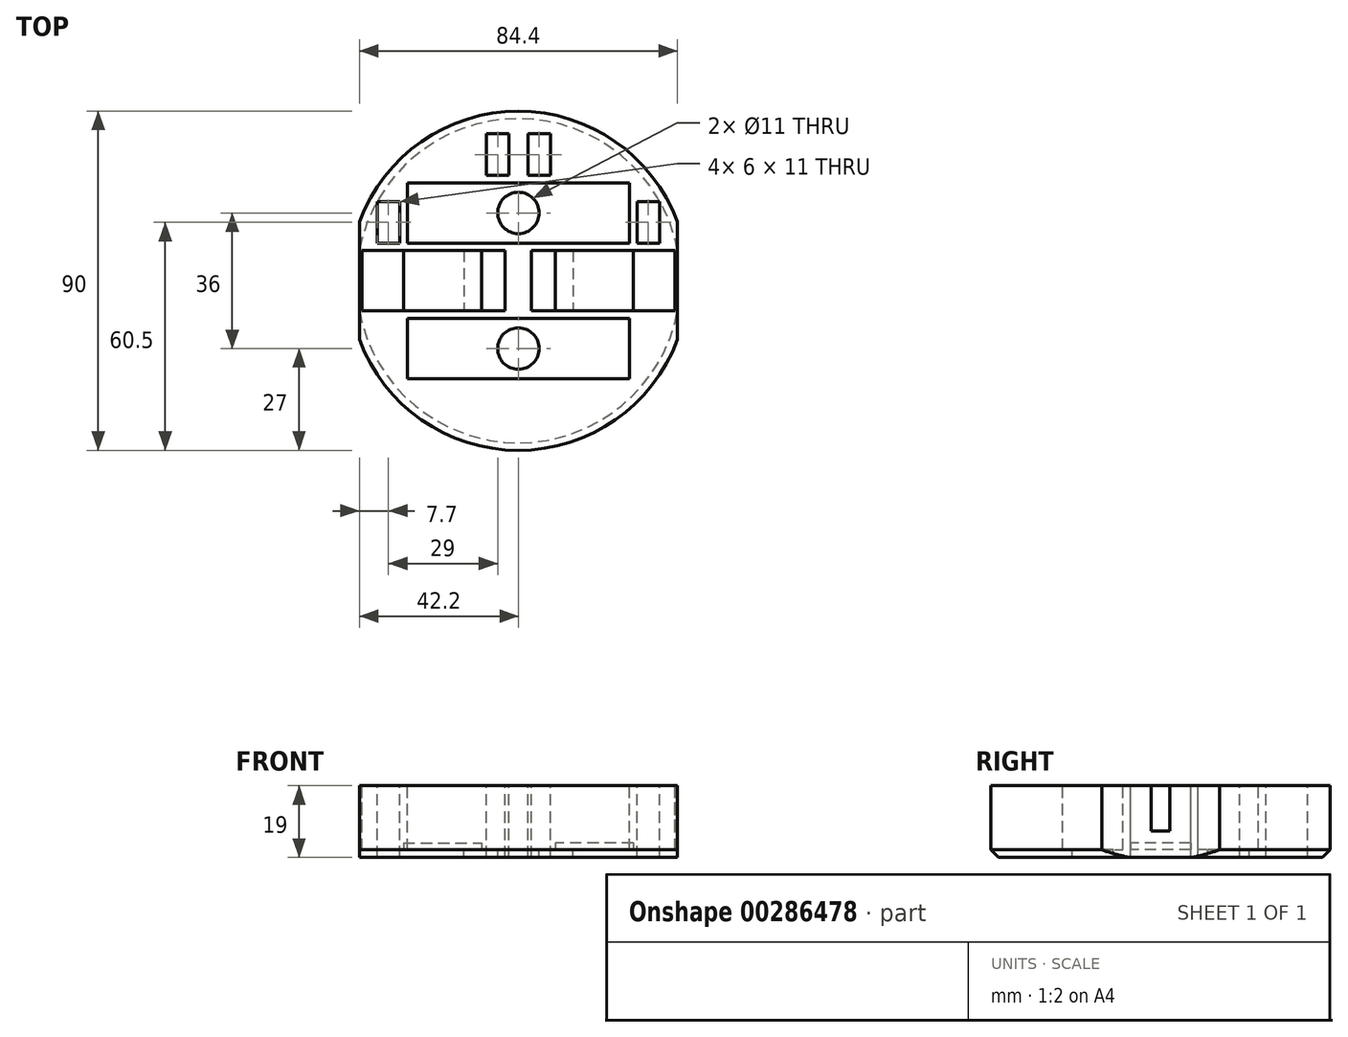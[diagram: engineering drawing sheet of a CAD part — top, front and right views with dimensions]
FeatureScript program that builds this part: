
annotation { "Feature Type Name" : "Feature", "Feature Type Description" : "" }
export const myFeature = defineFeature(function(context is Context, id is Id, definition is map)
    precondition{}
    {
        {
            var Q0;
            Q0=qCreatedBy(makeId("Top.planeOp"),FACE);
            var sketch = newSketch(context, id + "F0", { "sketchPlane" : qUnion([Q0])});
            skCircle(sketch, "E0", {"center": v(0, 0) * mm, "radius": 45 * mm});
            skSolve(sketch);
        }
        {
            var Q0;
            Q0=qSketchRegion(id+"F0",true);
            extrude(context, id + "F1", {"entities" : qUnion([Q0]), "depth" : 19 * mm, "offsetDistance" : 25 * mm});
        }
        {
            var Q0;
            Q0=makeQuery(id+"F1.opExtrude","CAP_FACE",FACE,{"disambiguationData":[OSD([sQuery(id+"F0.wireOp",EDGE,"E0")])],"isStart":false});
            var sketch = newSketch(context, id + "F2", { "sketchPlane" : qUnion([Q0])});
            skLineSegment(sketch, "E1.bottom", {"start": v(41.5, 8) * mm, "end": v(3.5, 8) * mm});
            skLineSegment(sketch, "E1.top", {"start": v(41.5, -8) * mm, "end": v(3.5, -8) * mm});
            skLineSegment(sketch, "E1.left", {"start": v(41.5, 8) * mm, "end": v(41.5, -8) * mm});
            skLineSegment(sketch, "E1.right", {"start": v(3.5, 8) * mm, "end": v(3.5, -8) * mm});
            skPoint(sketch, "E1.middle", {"position": v(22.5, 0) * mm});
            skLineSegment(sketch, "E2.bottom", {"start": v(41.5, 2.5) * mm, "end": v(48.5, 2.5) * mm});
            skLineSegment(sketch, "E2.top", {"start": v(41.5, -2.5) * mm, "end": v(48.5, -2.5) * mm});
            skLineSegment(sketch, "E2.left", {"start": v(41.5, 2.5) * mm, "end": v(41.5, -2.5) * mm});
            skLineSegment(sketch, "E2.right", {"start": v(48.5, 2.5) * mm, "end": v(48.5, -2.5) * mm});
            skPoint(sketch, "E2.middle", {"position": v(45, 0) * mm});
            skLineSegment(sketch, "E3.bottom", {"start": v(29.5, 26) * mm, "end": v(-29.5, 26) * mm});
            skLineSegment(sketch, "E3.top", {"start": v(29.5, 10) * mm, "end": v(-29.5, 10) * mm});
            skLineSegment(sketch, "E3.left", {"start": v(29.5, 26) * mm, "end": v(29.5, 10) * mm});
            skLineSegment(sketch, "E3.right", {"start": v(-29.5, 26) * mm, "end": v(-29.5, 10) * mm});
            skPoint(sketch, "E3.middle", {"position": v(0, 18) * mm});
            skLineSegment(sketch, "E4.MirrorCS", {"start": v(29.5, -10) * mm, "end": v(-29.5, -10) * mm});
            skLineSegment(sketch, "E5.MirrorCS", {"start": v(29.5, -26) * mm, "end": v(29.5, -10) * mm});
            skLineSegment(sketch, "E6.MirrorCS", {"start": v(29.5, -26) * mm, "end": v(-29.5, -26) * mm});
            skLineSegment(sketch, "E7.MirrorCS", {"start": v(-29.5, -26) * mm, "end": v(-29.5, -10) * mm});
            skLineSegment(sketch, "E8.MirrorCS", {"start": v(-41.5, 8) * mm, "end": v(-3.5, 8) * mm});
            skLineSegment(sketch, "E9.MirrorCS", {"start": v(-3.5, 8) * mm, "end": v(-3.5, -8) * mm});
            skLineSegment(sketch, "E10.MirrorCS", {"start": v(-41.5, -8) * mm, "end": v(-3.5, -8) * mm});
            skLineSegment(sketch, "E11.MirrorCS", {"start": v(-41.5, -2.5) * mm, "end": v(-48.5, -2.5) * mm});
            skLineSegment(sketch, "E12.MirrorCS", {"start": v(-48.5, 2.5) * mm, "end": v(-48.5, -2.5) * mm});
            skLineSegment(sketch, "E13.MirrorCS", {"start": v(-41.5, 2.5) * mm, "end": v(-48.5, 2.5) * mm});
            skLineSegment(sketch, "E14.MirrorCS", {"start": v(-41.5, 8) * mm, "end": v(-41.5, -8) * mm});
            skCircle(sketch, "E15", {"center": v(0, 0) * mm, "radius": 41.32 * mm, "construction": true});
            skSolve(sketch);
        }
        {
            var Q0;
            Q0=qSketchRegion(id+"F2",true);
            extrude(context, id + "F3", {"entities" : qUnion([Q0]), "operationType" : NewBodyOperationType.REMOVE, "oppositeDirection" : true, "depth" : 17 * mm, "offsetDistance" : 25 * mm});
        }
        {
            var Q0;
            Q0=makeQuery(id+"F1.opExtrude","CAP_FACE",FACE,{"disambiguationData":[OSD([sQuery(id+"F0.wireOp",EDGE,"E0")])],"isStart":false});
            var sketch = newSketch(context, id + "F4", { "sketchPlane" : qUnion([Q0])});
            skLineSegment(sketch, "E16.bottom", {"start": v(-37.5, 21) * mm, "end": v(-31.5, 21) * mm});
            skLineSegment(sketch, "E16.top", {"start": v(-37.5, 10) * mm, "end": v(-31.5, 10) * mm});
            skLineSegment(sketch, "E16.left", {"start": v(-37.5, 21) * mm, "end": v(-37.5, 10) * mm});
            skLineSegment(sketch, "E16.right", {"start": v(-31.5, 21) * mm, "end": v(-31.5, 10) * mm});
            skLineSegment(sketch, "E17.MirrorCS", {"start": v(37.5, 21) * mm, "end": v(37.5, 10) * mm});
            skLineSegment(sketch, "E18.MirrorCS", {"start": v(37.5, 10) * mm, "end": v(31.5, 10) * mm});
            skLineSegment(sketch, "E19.MirrorCS", {"start": v(37.5, 21) * mm, "end": v(31.5, 21) * mm});
            skLineSegment(sketch, "E20.MirrorCS", {"start": v(31.5, 21) * mm, "end": v(31.5, 10) * mm});
            skLineSegment(sketch, "E21.bottom", {"start": v(-8.5, 39) * mm, "end": v(-2.5, 39) * mm});
            skLineSegment(sketch, "E21.top", {"start": v(-8.5, 28) * mm, "end": v(-2.5, 28) * mm});
            skLineSegment(sketch, "E21.left", {"start": v(-8.5, 39) * mm, "end": v(-8.5, 28) * mm});
            skLineSegment(sketch, "E21.right", {"start": v(-2.5, 39) * mm, "end": v(-2.5, 28) * mm});
            skLineSegment(sketch, "E22.MirrorCS", {"start": v(8.5, 39) * mm, "end": v(2.5, 39) * mm});
            skLineSegment(sketch, "E23.MirrorCS", {"start": v(8.5, 39) * mm, "end": v(8.5, 28) * mm});
            skLineSegment(sketch, "E24.MirrorCS", {"start": v(2.5, 39) * mm, "end": v(2.5, 28) * mm});
            skLineSegment(sketch, "E25.MirrorCS", {"start": v(8.5, 28) * mm, "end": v(2.5, 28) * mm});
            skLineSegment(sketch, "E26.bottom", {"start": v(-3.5, 8) * mm, "end": v(-14.5, 8) * mm});
            skLineSegment(sketch, "E26.top", {"start": v(-3.5, -8) * mm, "end": v(-14.5, -8) * mm});
            skLineSegment(sketch, "E26.left", {"start": v(-3.5, 8) * mm, "end": v(-3.5, -8) * mm});
            skLineSegment(sketch, "E26.right", {"start": v(-14.5, 8) * mm, "end": v(-14.5, -8) * mm});
            skLineSegment(sketch, "E27.MirrorCS", {"start": v(3.5, 8) * mm, "end": v(3.5, -8) * mm});
            skLineSegment(sketch, "E28.MirrorCS", {"start": v(3.5, -8) * mm, "end": v(14.5, -8) * mm});
            skLineSegment(sketch, "E29.MirrorCS", {"start": v(3.5, 8) * mm, "end": v(14.5, 8) * mm});
            skLineSegment(sketch, "E30.MirrorCS", {"start": v(14.5, 8) * mm, "end": v(14.5, -8) * mm});
            skLineSegment(sketch, "E31.bottom", {"start": v(-42.2, 22.6) * mm, "end": v(-52.98, 22.6) * mm});
            skLineSegment(sketch, "E31.top", {"start": v(-42.2, -22.6) * mm, "end": v(-52.98, -22.6) * mm});
            skLineSegment(sketch, "E31.left", {"start": v(-42.2, 22.6) * mm, "end": v(-42.2, -22.6) * mm});
            skLineSegment(sketch, "E31.right", {"start": v(-52.98, 22.6) * mm, "end": v(-52.98, -22.6) * mm});
            skPoint(sketch, "E31.middle", {"position": v(-47.6, 0) * mm});
            skLineSegment(sketch, "E32.MirrorCS", {"start": v(42.2, 22.6) * mm, "end": v(52.98, 22.6) * mm});
            skLineSegment(sketch, "E33.MirrorCS", {"start": v(52.98, 22.6) * mm, "end": v(52.98, -22.6) * mm});
            skLineSegment(sketch, "E34.MirrorCS", {"start": v(42.2, 22.6) * mm, "end": v(42.2, -22.6) * mm});
            skLineSegment(sketch, "E35.MirrorCS", {"start": v(42.2, -22.6) * mm, "end": v(52.98, -22.6) * mm});
            skCircle(sketch, "E36", {"center": v(0, 18) * mm, "radius": 5.5 * mm});
            skPoint(sketch, "E36.centerSnap0", {"position": v(-29.5, 18) * mm});
            skCircle(sketch, "E37.MirrorC", {"center": v(0, -18) * mm, "radius": 5.5 * mm});
            skSolve(sketch);
        }
        {
            var Q0;
            Q0=qSketchRegion(id+"F4",true);
            extrude(context, id + "F5", {"entities" : qUnion([Q0]), "operationType" : NewBodyOperationType.REMOVE, "endBound" : BoundingType.THROUGH_ALL, "oppositeDirection" : true, "depth" : 25 * mm, "offsetDistance" : 25 * mm});
        }
        {
            var Q0;
            Q0=makeQuery(id+"F1.opExtrude","CAP_FACE",FACE,{"disambiguationData":[OSD([sQuery(id+"F0.wireOp",EDGE,"E0")])],"isStart":false});
            var sketch = newSketch(context, id + "F6", { "sketchPlane" : qUnion([Q0])});
            skLineSegment(sketch, "E38.bottom", {"start": v(-42.2, 2.5) * mm, "end": v(-41.5, 2.5) * mm});
            skLineSegment(sketch, "E38.top", {"start": v(-42.2, -2.5) * mm, "end": v(-41.5, -2.5) * mm});
            skLineSegment(sketch, "E38.left", {"start": v(-42.2, 2.5) * mm, "end": v(-42.2, -2.5) * mm});
            skLineSegment(sketch, "E38.right", {"start": v(-41.5, 2.5) * mm, "end": v(-41.5, -2.5) * mm});
            skLineSegment(sketch, "E39.MirrorCS", {"start": v(42.2, 2.5) * mm, "end": v(41.5, 2.5) * mm});
            skLineSegment(sketch, "E40.MirrorCS", {"start": v(42.2, -2.5) * mm, "end": v(41.5, -2.5) * mm});
            skLineSegment(sketch, "E41.MirrorCS", {"start": v(41.5, 2.5) * mm, "end": v(41.5, -2.5) * mm});
            skLineSegment(sketch, "E42.MirrorCS", {"start": v(42.2, 2.5) * mm, "end": v(42.2, -2.5) * mm});
            skSolve(sketch);
        }
        {
            var Q0;
            Q0 = qSketchRegion(id + "F6", true);
            extrude(context, id + "F7", {"entities" : qUnion([Q0]), "operationType" : NewBodyOperationType.ADD, "endBound" : BoundingType.UP_TO_NEXT, "oppositeDirection" : true, "depth" : 5 * mm, "offsetDistance" : 25 * mm, "hasSecondDirection" : true, "secondDirectionBound" : BoundingType.UP_TO_NEXT, "secondDirectionOppositeDirection" : true, "secondDirectionDepth" : 25 * mm, "hasSecondDirectionOffset" : true, "secondDirectionOffsetDistance" : 5 * mm});
        }
        {
            var Q0;
            Q0=makeQuery(id+"F3.boolean.opBoolean","COPY",FACE,{"derivedFrom":makeQuery(id+"F3.opExtrude","CAP_FACE",FACE,{"disambiguationData":[OSD([sQuery(id+"F2.wireOp",EDGE,"E8.MirrorCS"),sQuery(id+"F2.wireOp",EDGE,"E9.MirrorCS"),sQuery(id+"F2.wireOp",EDGE,"E10.MirrorCS"),sQuery(id+"F2.wireOp",EDGE,"E11.MirrorCS"),sQuery(id+"F2.wireOp",EDGE,"E12.MirrorCS"),sQuery(id+"F2.wireOp",EDGE,"E13.MirrorCS"),sQuery(id+"F2.wireOp",EDGE,"E14.MirrorCS")])],"isStart":false})});
            var sketch = newSketch(context, id + "F8", { "sketchPlane" : qUnion([Q0])});
            skLineSegment(sketch, "E43.bottom", {"start": v(-30.5, 8) * mm, "end": v(-9.82, 8) * mm});
            skLineSegment(sketch, "E43.top", {"start": v(-30.5, -8) * mm, "end": v(-9.82, -8) * mm});
            skLineSegment(sketch, "E43.left", {"start": v(-30.5, 8) * mm, "end": v(-30.5, -8) * mm});
            skLineSegment(sketch, "E43.right", {"start": v(-9.82, 8) * mm, "end": v(-9.82, -8) * mm});
            skPoint(sketch, "E44", {"position": v(-28, -8) * mm});
            skLineSegment(sketch, "E45.MirrorCS", {"start": v(30.5, 8) * mm, "end": v(30.5, -8) * mm});
            skLineSegment(sketch, "E46.MirrorCS", {"start": v(9.82, 8) * mm, "end": v(9.82, -8) * mm});
            skLineSegment(sketch, "E47.MirrorCS", {"start": v(30.5, 8) * mm, "end": v(9.82, 8) * mm});
            skLineSegment(sketch, "E48.MirrorCS", {"start": v(30.5, -8) * mm, "end": v(9.82, -8) * mm});
            skPoint(sketch, "E49.MirrorP", {"position": v(28, -8) * mm});
            skSolve(sketch);
        }
        {
            var Q0;
            Q0 = qSketchRegion(id + "F8", true);
            extrude(context, id + "F9", {"entities" : qUnion([Q0]), "operationType" : NewBodyOperationType.ADD, "depth" : 1.82 * mm, "offsetDistance" : 25 * mm});
        }
        {
            var Q0;
            Q0=makeQuery(id+"F5.boolean.opBoolean","SPLIT",EDGE,{"disambiguationData":[OD(0.0)],"derivedFrom":makeQuery(id+"F1.opExtrude","CAP_EDGE",EDGE,{"disambiguationData":[OSD([sQuery(id+"F0.wireOp",EDGE,"E0")])],"isStart":true})});
            var Q1;
            Q1=makeQuery(id+"F5.boolean.opBoolean","SPLIT",EDGE,{"disambiguationData":[OD(1.0)],"derivedFrom":makeQuery(id+"F1.opExtrude","CAP_EDGE",EDGE,{"disambiguationData":[OSD([sQuery(id+"F0.wireOp",EDGE,"E0")])],"isStart":true})});
            chamfer(context, id + "F10", {"entities" : qUnion([Q0, Q1]), "width" : 2 * mm, "tangentPropagation" : true});
        }
    });
